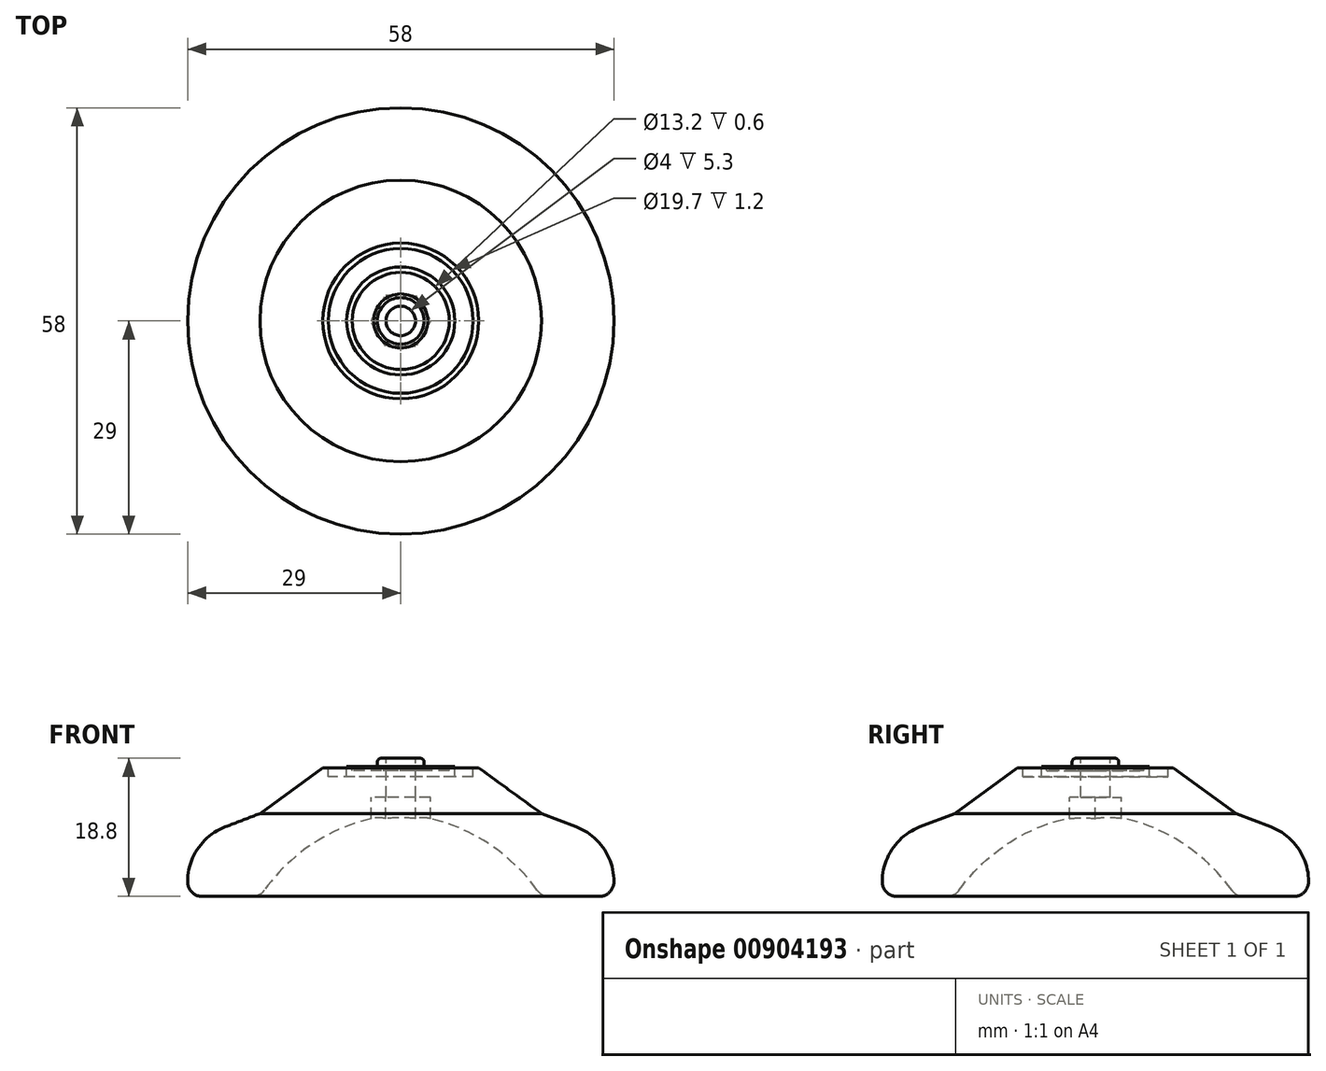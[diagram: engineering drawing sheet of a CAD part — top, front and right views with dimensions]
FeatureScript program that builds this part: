
annotation { "Feature Type Name" : "Feature", "Feature Type Description" : "" }
export const myFeature = defineFeature(function(context is Context, id is Id, definition is map)
    precondition{}
    {
        {
            var Q0;
            Q0=qCreatedBy(makeId("Front.planeOp"),FACE);
            var sketch = newSketch(context, id + "F0", { "sketchPlane" : qUnion([Q0])});
            skLineSegment(sketch, "E0", {"start": v(2, -1.2) * mm, "end": v(2, -9) * mm});
            skLineSegment(sketch, "E1", {"start": v(19.14, -20) * mm, "end": v(29, -20) * mm});
            skLineSegment(sketch, "E2", {"start": v(29, -20) * mm, "end": v(29, -12.5) * mm});
            skLineSegment(sketch, "E3", {"start": v(10.6, -2.5) * mm, "end": v(9.85, -2.5) * mm});
            skLineSegment(sketch, "E4", {"start": v(6.6, -2.3) * mm, "end": v(6.6, -2.9) * mm});
            skLineSegment(sketch, "E5", {"start": v(3.17, -2.4) * mm, "end": v(3.17, -1.2) * mm});
            skLineSegment(sketch, "E6", {"start": v(3.17, -1.2) * mm, "end": v(2, -1.2) * mm});
            skLineSegment(sketch, "E7", {"start": v(10.6, -2.5) * mm, "end": v(19.14, -8.71) * mm});
            skLineSegment(sketch, "E8", {"start": v(19.14, -8.71) * mm, "end": v(29, -12.5) * mm});
            skLineSegment(sketch, "E9", {"start": v(12.85, -10.95) * mm, "end": v(19.14, -20) * mm});
            skLineSegment(sketch, "E10", {"start": v(0, 6.34) * mm, "end": v(0, -21.05) * mm, "construction": true});
            skLineSegment(sketch, "E11", {"start": v(-13.85, 0) * mm, "end": v(41.9, 0) * mm, "construction": true});
            skLineSegment(sketch, "E12", {"start": v(3.17, -2.4) * mm, "end": v(3.67, -2.4) * mm});
            skLineSegment(sketch, "E13", {"start": v(3.67, -2.4) * mm, "end": v(3.67, -2.9) * mm});
            skLineSegment(sketch, "E14", {"start": v(3.67, -2.9) * mm, "end": v(6.6, -2.9) * mm});
            skLineSegment(sketch, "E15.top", {"start": v(7.35, -3.7) * mm, "end": v(9.85, -3.7) * mm});
            skLineSegment(sketch, "E15.left", {"start": v(7.35, -2.3) * mm, "end": v(7.35, -3.7) * mm});
            skLineSegment(sketch, "E15.right", {"start": v(9.85, -2.5) * mm, "end": v(9.85, -3.7) * mm});
            skLineSegment(sketch, "E16.trimOffspring", {"start": v(7.35, -2.3) * mm, "end": v(6.6, -2.3) * mm});
            skLineSegment(sketch, "E17.top", {"start": v(12.85, -10.95) * mm, "end": v(2, -9) * mm});
            skSolve(sketch);
        }
        {
            var Q0;
            Q0=makeQuery(id+"F0.imprint","IMPRINT",FACE,{"disambiguationData":[TD([[makeQuery(id+"F0.imprint","IMPRINT",EDGE,{"derivedFrom":sQuery(id+"F0.wireOp",EDGE,"E0")}),1.0]])]});
            var Q1;
            Q1=sQuery(id+"F0.wireOp",EDGE,"E10");
            revolve(context, id + "F1", {"surfaceOperationType" : NewSurfaceOperationType.NEW, "entities" : qUnion([Q0]), "axis" : qUnion([Q1]), "revolveType" : RevolveType.FULL});
        }
        {
            var Q0;
            Q0=makeQuery(id+"F1.opRevolve","SWEPT_EDGE",EDGE,{"disambiguationData":[OSD([sQuery(id+"F0.wireOp",EDGE,"1Bdlj7cP-P2vO-Xs4z-yuBC-cHIkbWSHZuql"),sQuery(id+"F0.wireOp",EDGE,"9dAODfWi-b5Gm-Zpj9-cOzx-UoIZbGRsIp8L")])]});
            var Q1;
            Q1=makeQuery(id+"F1.opRevolve","SWEPT_EDGE",EDGE,{"disambiguationData":[OSD([sQuery(id+"F0.wireOp",EDGE,"E9"),sQuery(id+"F0.wireOp",EDGE,"E17.top")])]});
            fillet(context, id + "F2", {"entities" : qUnion([Q0, Q1]), "radius" : 25 * mm, "tangentPropagation" : true, "allowEdgeOverflow" : false});
        }
        {
            var Q0;
            Q0=makeQuery(id+"F1.opRevolve","SWEPT_EDGE",EDGE,{"disambiguationData":[OSD([sQuery(id+"F0.wireOp",EDGE,"E2"),sQuery(id+"F0.wireOp",EDGE,"E8")])]});
            fillet(context, id + "F3", {"entities" : qUnion([Q0]), "radius" : 8 * mm, "tangentPropagation" : true, "allowEdgeOverflow" : false});
        }
        {
            var Q0;
            Q0=makeQuery(id+"F1.opRevolve","SWEPT_EDGE",EDGE,{"disambiguationData":[OSD([sQuery(id+"F0.wireOp",EDGE,"E5"),sQuery(id+"F0.wireOp",EDGE,"E6")])]});
            fillet(context, id + "F4", {"entities" : qUnion([Q0]), "radius" : .5 * mm, "tangentPropagation" : true, "allowEdgeOverflow" : false});
        }
        {
            var Q0;
            Q0=makeQuery(id+"F1.opRevolve","SWEPT_EDGE",EDGE,{"disambiguationData":[OSD([sQuery(id+"F0.wireOp",EDGE,"E1"),sQuery(id+"F0.wireOp",EDGE,"E2")])]});
            var Q1;
            Q1=makeQuery(id+"F1.opRevolve","SWEPT_EDGE",EDGE,{"disambiguationData":[OSD([sQuery(id+"F0.wireOp",EDGE,"E1"),sQuery(id+"F0.wireOp",EDGE,"E9")])]});
            fillet(context, id + "F5", {"entities" : qUnion([Q0, Q1]), "radius" : 2 * mm, "tangentPropagation" : true, "allowEdgeOverflow" : false});
        }
        {
            var Q0;
            Q0=qCreatedBy(makeId("Top.planeOp"),FACE);
            cPlane(context, id + "F6", {"entities" : qUnion([Q0]), "cplaneType" : CPlaneType.OFFSET, "offset" : 6.5 * mm, "oppositeDirection" : true, "width" : 150 * mm, "height" : 150 * mm});
        }
        {
            var Q0;
            Q0=qCreatedBy(id+"F6.planeOp",FACE);
            var sketch = newSketch(context, id + "F7", { "sketchPlane" : qUnion([Q0])});
            skCircle(sketch, "E18.cCircle", {"center": v(0, 0) * mm, "radius": 3.5 * mm, "construction": true});
            skLineSegment(sketch, "E18.0", {"start": v(4.04, 0) * mm, "end": v(2.02, -3.5) * mm});
            skLineSegment(sketch, "E18.1", {"start": v(2.02, -3.5) * mm, "end": v(-2.02, -3.5) * mm});
            skLineSegment(sketch, "E18.2", {"start": v(-2.02, -3.5) * mm, "end": v(-4.04, 0) * mm});
            skLineSegment(sketch, "E18.3", {"start": v(-4.04, 0) * mm, "end": v(-2.02, 3.5) * mm});
            skLineSegment(sketch, "E18.4", {"start": v(-2.02, 3.5) * mm, "end": v(2.02, 3.5) * mm});
            skLineSegment(sketch, "E18.5", {"start": v(2.02, 3.5) * mm, "end": v(4.04, 0) * mm});
            skPoint(sketch, "E18.0.midPoint", {"position": v(3.03, -1.75) * mm});
            skSolve(sketch);
        }
        {
            var Q0;
            Q0=makeQuery(id+"F7.imprint","IMPRINT",FACE,{"disambiguationData":[TD([[makeQuery(id+"F7.imprint","IMPRINT",EDGE,{"derivedFrom":sQuery(id+"F7.wireOp",EDGE,"E18.0")}),-1.0]])]});
            extrude(context, id + "F8", {"entities" : qUnion([Q0]), "operationType" : NewBodyOperationType.REMOVE, "oppositeDirection" : true, "depth" : 3.5 * mm, "offsetDistance" : 25 * mm});
        }
    });
